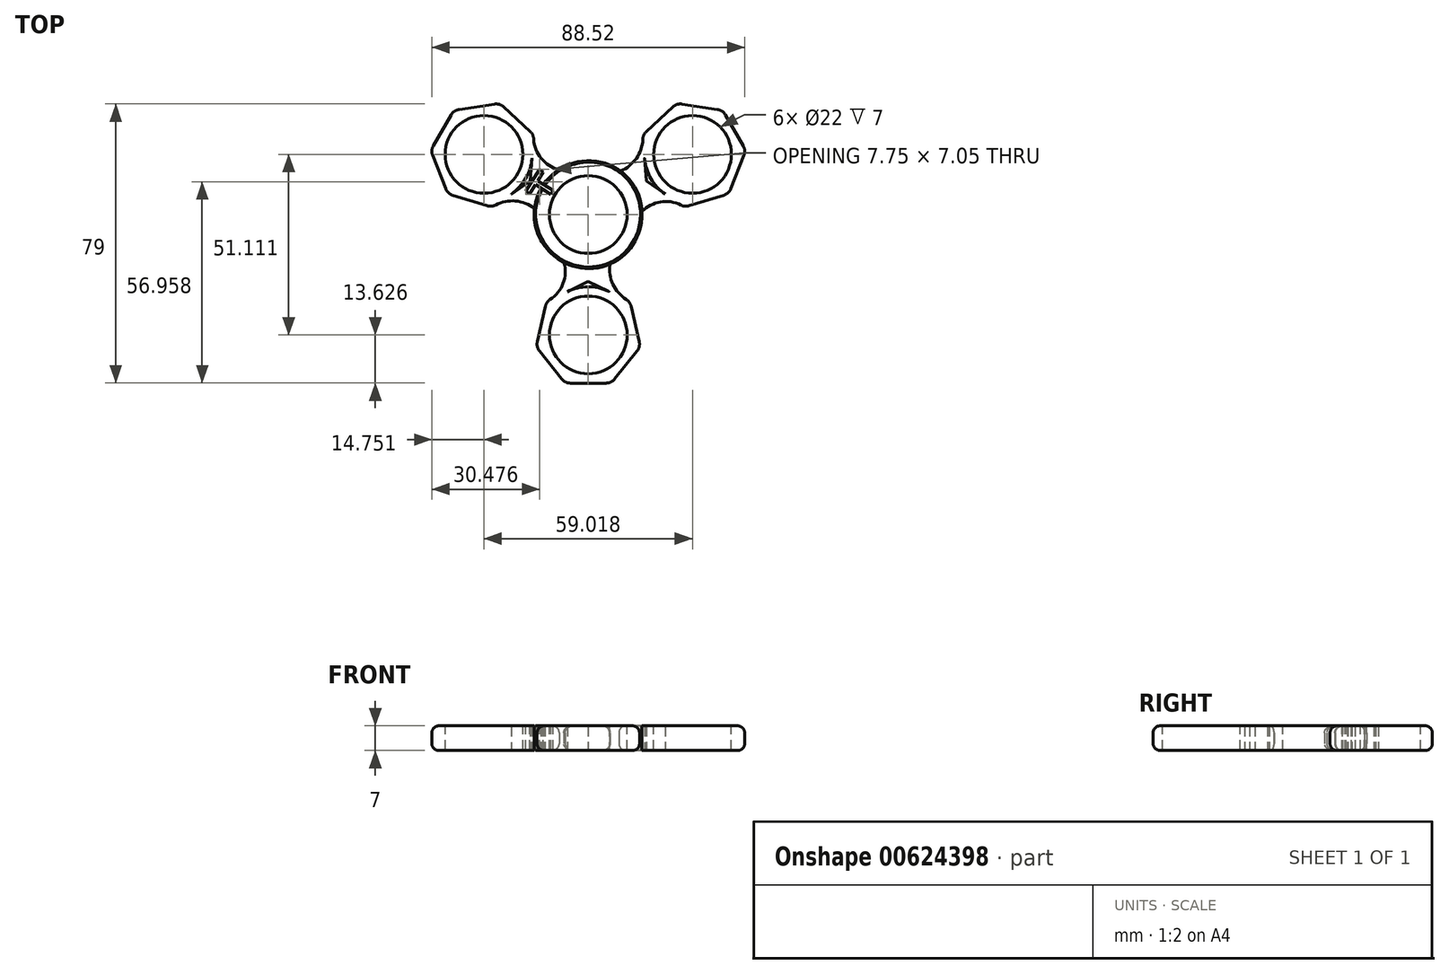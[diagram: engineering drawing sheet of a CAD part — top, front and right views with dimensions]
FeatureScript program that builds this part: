
annotation { "Feature Type Name" : "Feature", "Feature Type Description" : "" }
export const myFeature = defineFeature(function(context is Context, id is Id, definition is map)
    precondition{}
    {
        {
            var Q0;
            Q0=qCreatedBy(makeId("Top.planeOp"),FACE);
            var sketch = newSketch(context, id + "F0", { "sketchPlane" : qUnion([Q0])});
            skCircle(sketch, "E0", {"center": v(0, -34.07) * mm, "radius": 13.63 * mm});
            skCircle(sketch, "E1.cCircle", {"center": v(0, -34.07) * mm, "radius": 13.63 * mm, "construction": true});
            skLineSegment(sketch, "E1.0", {"start": v(6.56, -47.7) * mm, "end": v(-6.56, -47.7) * mm});
            skLineSegment(sketch, "E1.1", {"start": v(-6.56, -47.7) * mm, "end": v(-14.75, -37.44) * mm});
            skLineSegment(sketch, "E1.2", {"start": v(-14.75, -37.44) * mm, "end": v(-11.83, -24.64) * mm});
            skLineSegment(sketch, "E1.3", {"start": v(-11.83, -24.64) * mm, "end": v(0, -18.95) * mm});
            skLineSegment(sketch, "E1.4", {"start": v(0, -18.95) * mm, "end": v(11.83, -24.64) * mm});
            skLineSegment(sketch, "E1.5", {"start": v(11.83, -24.64) * mm, "end": v(14.75, -37.44) * mm});
            skLineSegment(sketch, "E1.6", {"start": v(14.75, -37.44) * mm, "end": v(6.56, -47.7) * mm});
            skPoint(sketch, "E1.0.midPoint", {"position": v(0, -47.7) * mm});
            skPoint(sketch, "E2.0.midPoint", {"position": v(0, -13.63) * mm});
            skArc(sketch, "E3", {"start": v(6.18, -13.57) * mm, "mid": v(-0.16, 15.1) * mm, "end": v(-6.92, -13.47) * mm});
            skArc(sketch, "E4", {"start": v(-11.83, -24.64) * mm, "mid": v(-7.3, -19.96) * mm, "end": v(-6.92, -13.47) * mm});
            skArc(sketch, "E5", {"start": v(6.18, -13.57) * mm, "mid": v(7.14, -20.06) * mm, "end": v(11.83, -24.64) * mm});
            skLineSegment(sketch, "E6", {"start": v(6.18, -13.57) * mm, "end": v(4.84, -13.57) * mm});
            skLineSegment(sketch, "E7", {"start": v(-6.92, -13.47) * mm, "end": v(-5.57, -13.47) * mm});
            skArc(sketch, "E8", {"start": v(-8.64, -23.1) * mm, "mid": v(-5.6, -18.77) * mm, "end": v(-5.57, -13.47) * mm});
            skArc(sketch, "E9", {"start": v(4.84, -13.57) * mm, "mid": v(4.8, -17.86) * mm, "end": v(6.18, -21.92) * mm});
            skSolve(sketch);
        }
        {
            var Q0;
            Q0 = qSketchRegion(id + "F0", true);
            var Q1;
            Q1 = qSketchRegion(id + "F2", true);
            extrude(context, id + "F1", {"entities" : qUnion([Q0, Q1]), "depth" : 7 * mm, "offsetDistance" : 25 * mm});
        }
        {
            var Q0;
            Q0=makeQuery(id+"F1.opExtrude","CAP_FACE",FACE,{"disambiguationData":[OSD([sQuery(id+"F0.wireOp",EDGE,"86ABmI6o-ZAT3-Tekt-z6PM-mWoQ0BzI8RFv"),sQuery(id+"F0.wireOp",EDGE,"E0"),sQuery(id+"F0.wireOp",EDGE,"QfQ5Vzes-D5an-T3km-K8pF-N7WL8GsApWXA"),sQuery(id+"F0.wireOp",EDGE,"wE60L3jZ-py04-XnBw-GZlh-51vzE29tedhQ")])],"isStart":false});
            var sketch = newSketch(context, id + "F2", { "sketchPlane" : qUnion([Q0])});
            skCircle(sketch, "E10", {"center": v(0, 0) * mm, "radius": 11 * mm});
            skCircle(sketch, "E11", {"center": v(0, -34.07) * mm, "radius": 11 * mm});
            skSolve(sketch);
        }
        {
            var Q0;
            Q0 = qSketchRegion(id + "F2", true);
            extrude(context, id + "F3", {"entities" : qUnion([Q0]), "operationType" : NewBodyOperationType.REMOVE, "endBound" : BoundingType.THROUGH_ALL, "oppositeDirection" : true, "depth" : 7 * mm, "offsetDistance" : 25 * mm});
        }
        {
            var Q0;
            Q0=qCreatedBy(makeId("Front.planeOp"),FACE);
            var sketch = newSketch(context, id + "F4", { "sketchPlane" : qUnion([Q0])});
            skLineSegment(sketch, "E12", {"start": v(0, 0) * mm, "end": v(0, 20.09) * mm});
            skSolve(sketch);
        }
        {
            var Q0;
            Q0=makeQuery(id+"F1.opExtrude","SWEPT_BODY",BODY,{"disambiguationData":[OSD([sQuery(id+"F0.wireOp",EDGE,"86ABmI6o-ZAT3-Tekt-z6PM-mWoQ0BzI8RFv"),sQuery(id+"F0.wireOp",EDGE,"E0"),sQuery(id+"F0.wireOp",EDGE,"QfQ5Vzes-D5an-T3km-K8pF-N7WL8GsApWXA"),sQuery(id+"F0.wireOp",EDGE,"wE60L3jZ-py04-XnBw-GZlh-51vzE29tedhQ")])]});
            var Q1;
            Q1=sQuery(id+"F4.wireOp",EDGE,"E12");
            circularPattern(context, id + "F5", {"entities" : qUnion([Q0]), "axis" : qUnion([Q1]), "angle" : 360 * degree, "instanceCount" : 3, "equalSpace" : true});
        }
        {
            var Q0;
            Q0=makeQuery(id+"F5.opPattern","COPY",EDGE,{"derivedFrom":makeQuery(id+"F1.opExtrude","SWEPT_EDGE",EDGE,{"disambiguationData":[OSD([sQuery(id+"F0.wireOp",EDGE,"E1.0"),sQuery(id+"F0.wireOp",EDGE,"E1.6")])]}),"instanceName":"2"});
            var Q1;
            Q1=makeQuery(id+"F5.opPattern","COPY",EDGE,{"derivedFrom":makeQuery(id+"F1.opExtrude","SWEPT_EDGE",EDGE,{"disambiguationData":[OSD([sQuery(id+"F0.wireOp",EDGE,"E1.0"),sQuery(id+"F0.wireOp",EDGE,"E1.1")])]}),"instanceName":"2"});
            var Q2;
            Q2=makeQuery(id+"F5.opPattern","COPY",EDGE,{"derivedFrom":makeQuery(id+"F1.opExtrude","SWEPT_EDGE",EDGE,{"disambiguationData":[OSD([sQuery(id+"F0.wireOp",EDGE,"E1.1"),sQuery(id+"F0.wireOp",EDGE,"E1.2")])]}),"instanceName":"2"});
            var Q3;
            Q3=makeQuery(id+"F5.opPattern","COPY",EDGE,{"derivedFrom":makeQuery(id+"F1.opExtrude","SWEPT_EDGE",EDGE,{"disambiguationData":[OSD([sQuery(id+"F0.wireOp",EDGE,"E1.5"),sQuery(id+"F0.wireOp",EDGE,"E1.6")])]}),"instanceName":"2"});
            var Q4;
            Q4=makeQuery(id+"F5.opPattern","COPY",EDGE,{"derivedFrom":makeQuery(id+"F1.opExtrude","SWEPT_EDGE",EDGE,{"disambiguationData":[OSD([sQuery(id+"F0.wireOp",EDGE,"E1.4"),sQuery(id+"F0.wireOp",EDGE,"E1.5"),sQuery(id+"F0.wireOp",EDGE,"E5")])]}),"instanceName":"2"});
            var Q5;
            Q5=makeQuery(id+"F5.opPattern","COPY",EDGE,{"derivedFrom":makeQuery(id+"F1.opExtrude","SWEPT_EDGE",EDGE,{"disambiguationData":[OSD([sQuery(id+"F0.wireOp",EDGE,"E1.2"),sQuery(id+"F0.wireOp",EDGE,"E1.3"),sQuery(id+"F0.wireOp",EDGE,"E4")])]}),"instanceName":"2"});
            var Q6;
            Q6=makeQuery(id+"F5.opPattern","COPY",EDGE,{"derivedFrom":makeQuery(id+"F1.opExtrude","SWEPT_EDGE",EDGE,{"disambiguationData":[OSD([sQuery(id+"F0.wireOp",EDGE,"E1.4"),sQuery(id+"F0.wireOp",EDGE,"E1.5"),sQuery(id+"F0.wireOp",EDGE,"E5")])]}),"instanceName":"1"});
            var Q7;
            Q7=makeQuery(id+"F5.opPattern","COPY",EDGE,{"derivedFrom":makeQuery(id+"F1.opExtrude","SWEPT_EDGE",EDGE,{"disambiguationData":[OSD([sQuery(id+"F0.wireOp",EDGE,"E1.5"),sQuery(id+"F0.wireOp",EDGE,"E1.6")])]}),"instanceName":"1"});
            var Q8;
            Q8=makeQuery(id+"F5.opPattern","COPY",EDGE,{"derivedFrom":makeQuery(id+"F1.opExtrude","SWEPT_EDGE",EDGE,{"disambiguationData":[OSD([sQuery(id+"F0.wireOp",EDGE,"E1.0"),sQuery(id+"F0.wireOp",EDGE,"E1.6")])]}),"instanceName":"1"});
            var Q9;
            Q9=makeQuery(id+"F5.opPattern","COPY",EDGE,{"derivedFrom":makeQuery(id+"F1.opExtrude","SWEPT_EDGE",EDGE,{"disambiguationData":[OSD([sQuery(id+"F0.wireOp",EDGE,"E1.0"),sQuery(id+"F0.wireOp",EDGE,"E1.1")])]}),"instanceName":"1"});
            var Q10;
            Q10=makeQuery(id+"F5.opPattern","COPY",EDGE,{"derivedFrom":makeQuery(id+"F1.opExtrude","SWEPT_EDGE",EDGE,{"disambiguationData":[OSD([sQuery(id+"F0.wireOp",EDGE,"E1.1"),sQuery(id+"F0.wireOp",EDGE,"E1.2")])]}),"instanceName":"1"});
            var Q11;
            Q11=makeQuery(id+"F5.opPattern","COPY",EDGE,{"derivedFrom":makeQuery(id+"F1.opExtrude","SWEPT_EDGE",EDGE,{"disambiguationData":[OSD([sQuery(id+"F0.wireOp",EDGE,"E1.2"),sQuery(id+"F0.wireOp",EDGE,"E1.3"),sQuery(id+"F0.wireOp",EDGE,"E4")])]}),"instanceName":"1"});
            var Q12;
            Q12=makeQuery(id+"F1.opExtrude","SWEPT_EDGE",EDGE,{"disambiguationData":[OSD([sQuery(id+"F0.wireOp",EDGE,"E1.4"),sQuery(id+"F0.wireOp",EDGE,"E1.5"),sQuery(id+"F0.wireOp",EDGE,"E5")])]});
            var Q13;
            Q13=makeQuery(id+"F1.opExtrude","SWEPT_EDGE",EDGE,{"disambiguationData":[OSD([sQuery(id+"F0.wireOp",EDGE,"E1.5"),sQuery(id+"F0.wireOp",EDGE,"E1.6")])]});
            var Q14;
            Q14=makeQuery(id+"F1.opExtrude","SWEPT_EDGE",EDGE,{"disambiguationData":[OSD([sQuery(id+"F0.wireOp",EDGE,"E1.0"),sQuery(id+"F0.wireOp",EDGE,"E1.6")])]});
            var Q15;
            Q15=makeQuery(id+"F1.opExtrude","SWEPT_EDGE",EDGE,{"disambiguationData":[OSD([sQuery(id+"F0.wireOp",EDGE,"E1.0"),sQuery(id+"F0.wireOp",EDGE,"E1.1")])]});
            var Q16;
            Q16=makeQuery(id+"F1.opExtrude","SWEPT_EDGE",EDGE,{"disambiguationData":[OSD([sQuery(id+"F0.wireOp",EDGE,"E1.1"),sQuery(id+"F0.wireOp",EDGE,"E1.2")])]});
            var Q17;
            Q17=makeQuery(id+"F1.opExtrude","SWEPT_EDGE",EDGE,{"disambiguationData":[OSD([sQuery(id+"F0.wireOp",EDGE,"E1.2"),sQuery(id+"F0.wireOp",EDGE,"E1.3"),sQuery(id+"F0.wireOp",EDGE,"E4")])]});
            fillet(context, id + "F6", {"entities" : qUnion([Q0, Q1, Q2, Q3, Q4, Q5, Q6, Q7, Q8, Q9, Q10, Q11, Q12, Q13, Q14, Q15, Q16, Q17]), "radius" : 3.1 * mm, "tangentPropagation" : true, "allowEdgeOverflow" : false});
        }
        {
            var Q0;
            Q0=makeQuery(id+"F5.opPattern","COPY",EDGE,{"derivedFrom":makeQuery(id+"F1.opExtrude","CAP_EDGE",EDGE,{"disambiguationData":[OSD([sQuery(id+"F0.wireOp",EDGE,"E1.2")])],"isStart":false}),"instanceName":"2"});
            var Q1;
            Q1=makeQuery(id+"F5.opPattern","COPY",EDGE,{"derivedFrom":makeQuery(id+"F1.opExtrude","CAP_EDGE",EDGE,{"disambiguationData":[OSD([sQuery(id+"F0.wireOp",EDGE,"E1.6")])],"isStart":false}),"instanceName":"1"});
            var Q2;
            Q2=makeQuery(id+"F1.opExtrude","CAP_EDGE",EDGE,{"disambiguationData":[OSD([sQuery(id+"F0.wireOp",EDGE,"E1.5")])],"isStart":true});
            var Q3;
            Q3=makeQuery(id+"F1.opExtrude","CAP_EDGE",EDGE,{"disambiguationData":[OSD([sQuery(id+"F0.wireOp",EDGE,"E1.6")])],"isStart":true});
            var Q4;
            Q4=makeQuery(id+"F1.opExtrude","CAP_EDGE",EDGE,{"disambiguationData":[OSD([sQuery(id+"F0.wireOp",EDGE,"E1.0")])],"isStart":true});
            var Q5;
            Q5=makeQuery(id+"F1.opExtrude","CAP_EDGE",EDGE,{"disambiguationData":[OSD([sQuery(id+"F0.wireOp",EDGE,"E1.1")])],"isStart":true});
            var Q6;
            Q6=makeQuery(id+"F1.opExtrude","CAP_EDGE",EDGE,{"disambiguationData":[OSD([sQuery(id+"F0.wireOp",EDGE,"E1.2")])],"isStart":false});
            var Q7;
            Q7=makeQuery(id+"F5.opPattern","COPY",EDGE,{"derivedFrom":makeQuery(id+"F1.opExtrude","CAP_EDGE",EDGE,{"disambiguationData":[OSD([sQuery(id+"F0.wireOp",EDGE,"E1.2")])],"isStart":true}),"instanceName":"1"});
            var Q8;
            Q8=makeQuery(id+"F5.opPattern","COPY",EDGE,{"derivedFrom":makeQuery(id+"F1.opExtrude","CAP_EDGE",EDGE,{"disambiguationData":[OSD([sQuery(id+"F0.wireOp",EDGE,"E1.5")])],"isStart":true}),"instanceName":"2"});
            fillet(context, id + "F7", {"entities" : qUnion([Q0, Q1, Q2, Q3, Q4, Q5, Q6, Q7, Q8]), "radius" : 2 * mm, "tangentPropagation" : true, "allowEdgeOverflow" : false});
        }
        {
            var Q0;
            Q0=makeQuery(id+"F5.opPattern","COPY",FACE,{"derivedFrom":makeQuery(id+"F1.opExtrude","CAP_FACE",FACE,{"disambiguationData":[OSD([sQuery(id+"F0.wireOp",EDGE,"E0"),sQuery(id+"F0.wireOp",EDGE,"E1.0"),sQuery(id+"F0.wireOp",EDGE,"E1.1"),sQuery(id+"F0.wireOp",EDGE,"E1.2"),sQuery(id+"F0.wireOp",EDGE,"E1.3"),sQuery(id+"F0.wireOp",EDGE,"E1.4"),sQuery(id+"F0.wireOp",EDGE,"E1.5"),sQuery(id+"F0.wireOp",EDGE,"E1.6"),sQuery(id+"F0.wireOp",EDGE,"E3"),sQuery(id+"F0.wireOp",EDGE,"E4"),sQuery(id+"F0.wireOp",EDGE,"E5")])],"isStart":false}),"instanceName":"2"});
            var sketch = newSketch(context, id + "F8", { "sketchPlane" : qUnion([Q0])});
            skLineSegment(sketch, "E13", {"start": v(-13.8, 12.78) * mm, "end": v(-17.66, 6.58) * mm});
            skLineSegment(sketch, "E14", {"start": v(-17.66, 6.58) * mm, "end": v(-16.55, 5.9) * mm});
            skLineSegment(sketch, "E15", {"start": v(-16.55, 5.9) * mm, "end": v(-14.97, 8.45) * mm});
            skLineSegment(sketch, "E16", {"start": v(-14.97, 8.45) * mm, "end": v(-10.6, 5.73) * mm});
            skLineSegment(sketch, "E17", {"start": v(-10.6, 5.73) * mm, "end": v(-9.91, 6.84) * mm});
            skLineSegment(sketch, "E18", {"start": v(-9.91, 6.84) * mm, "end": v(-14.29, 9.55) * mm});
            skLineSegment(sketch, "E19", {"start": v(-14.29, 9.55) * mm, "end": v(-12.7, 12.1) * mm});
            skLineSegment(sketch, "E20", {"start": v(-13.8, 12.78) * mm, "end": v(-12.7, 12.1) * mm});
            skSolve(sketch);
        }
        {
            var Q0;
            Q0 = qSketchRegion(id + "F8", true);
            var Q1;
            Q1=makeQuery(id+"F8.imprint","IMPRINT",FACE,{"disambiguationData":[TD([[makeQuery(id+"F8.imprint","IMPRINT",EDGE,{"derivedFrom":makeQuery(id+"F5.opPattern","COPY",EDGE,{"derivedFrom":makeQuery(id+"F3.boolean.opBoolean","COPY",EDGE,{"derivedFrom":makeQuery(id+"F3.opExtrude","CAP_EDGE",EDGE,{"disambiguationData":[OSD([sQuery(id+"F2.wireOp",EDGE,"E10")])],"isStart":true})}),"instanceName":"2"})}),1.0]])]});
            extrude(context, id + "F9", {"entities" : qUnion([Q0, Q1]), "operationType" : NewBodyOperationType.REMOVE, "endBound" : BoundingType.THROUGH_ALL, "oppositeDirection" : true, "depth" : 25 * mm, "offsetDistance" : 25 * mm});
        }
    });
